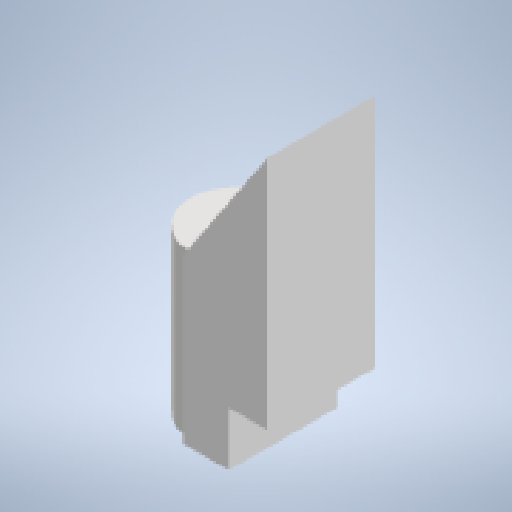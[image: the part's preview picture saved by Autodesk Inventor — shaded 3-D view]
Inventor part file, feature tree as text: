
AUTODESK INVENTOR PART (.ipt)
format: ipt  version: 2025 (Build 290162000, 162)  size: 270,336 bytes
history: native  units: mm
features: extrude x7, sketch x2
ambient origin geometry x8: Origin, YZ Plane, XZ Plane, XY Plane, X Axis, Y Axis, Z Axis, Center Point
bodies: Body1 (feature_tree)
feature tree (9):
  sketch  "Szkic1"
  extrude  "Wyciągnięcie proste4"  Depth=8.2mm
  extrude  "Wyciągnięcie proste5"  Depth=14.0mm
  extrude  "Wyciągnięcie proste6"  Depth=11.0mm
  extrude  "Wyciągnięcie proste7"  Depth=7.0mm
  extrude  "Wyciągnięcie proste8"  TaperAngle=0.0deg  [1 undecoded]
  extrude  "Wyciągnięcie proste9"  Depth=5.0mm
  extrude  "Wyciągnięcie proste10"  Depth=12.0mm
  sketch  "Szkic5"
note: 1 required parameter value undecoded (feature->parameter linkage not recoverable at this tier; creation-order binding heuristic only, values carry confidence <= 0.55)
